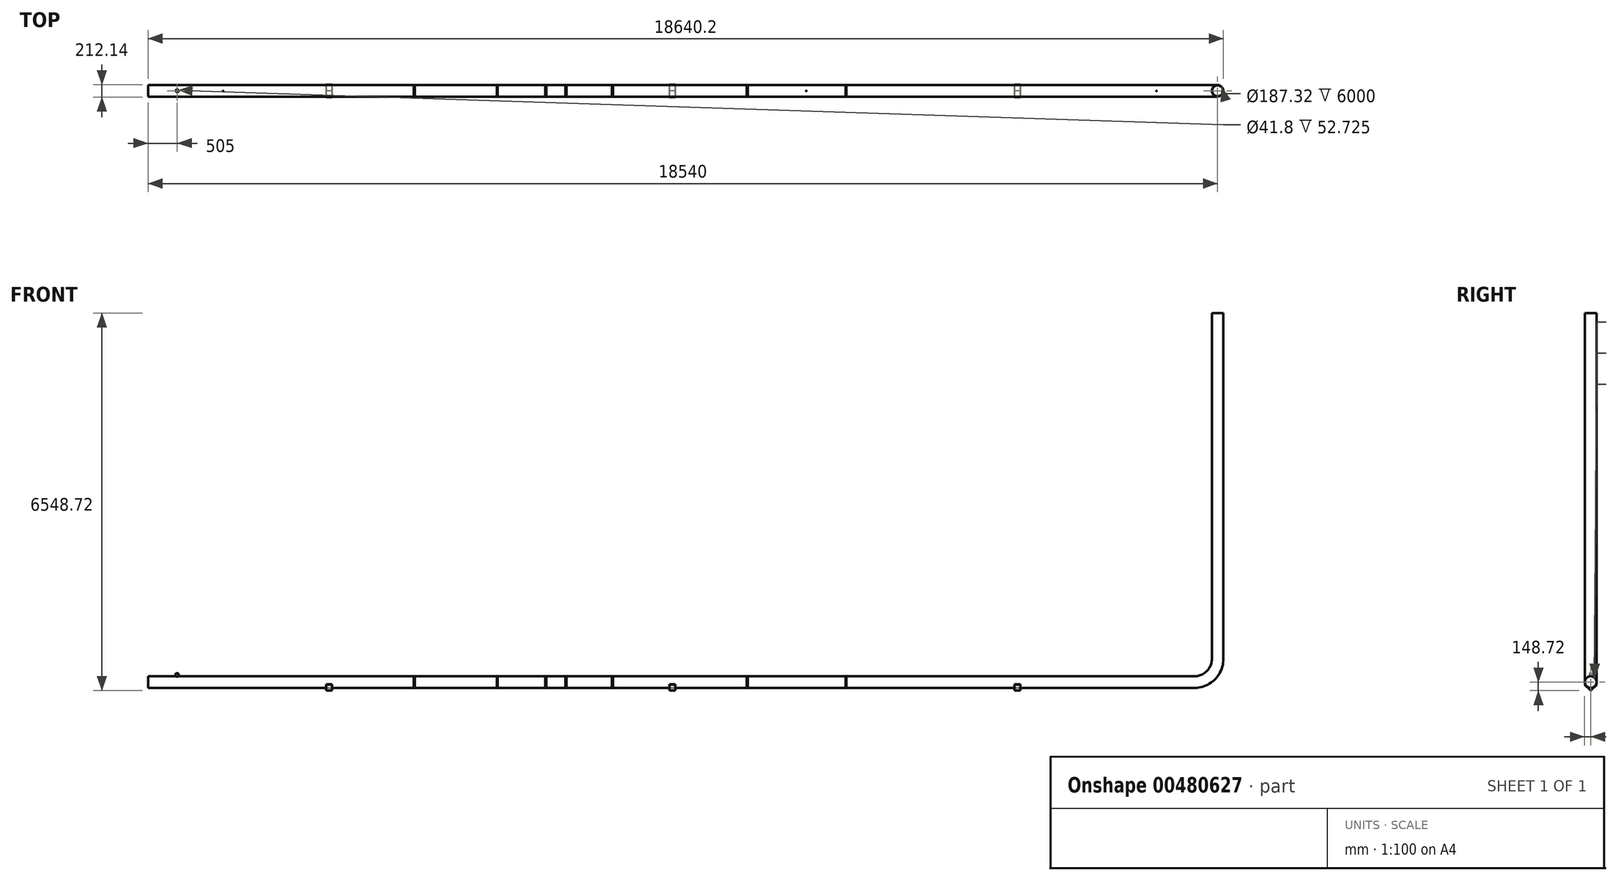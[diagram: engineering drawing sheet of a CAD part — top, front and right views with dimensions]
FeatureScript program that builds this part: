
annotation { "Feature Type Name" : "Feature", "Feature Type Description" : "" }
export const myFeature = defineFeature(function(context is Context, id is Id, definition is map)
    precondition{}
    {
        {
            var Q0;
            Q0=qCreatedBy(makeId("Right.planeOp"),FACE);
            var sketch = newSketch(context, id + "F0", { "sketchPlane" : qUnion([Q0])});
            skCircle(sketch, "E0", {"center": v(0, 0) * mm, "radius": 100.16 * mm});
            skCircle(sketch, "E1", {"center": v(0, 0) * mm, "radius": 93.66 * mm});
            skSolve(sketch);
        }
        {
            var Q0;
            Q0=qCreatedBy(makeId("Front.planeOp"),FACE);
            var sketch = newSketch(context, id + "F1", { "sketchPlane" : qUnion([Q0])});
            skLineSegment(sketch, "E2", {"start": v(0, 0) * mm, "end": v(18140, 0) * mm});
            skArc(sketch, "E3", {"start": v(18140, 0) * mm, "mid": v(18422.84, 117.16) * mm, "end": v(18540, 400) * mm});
            skLineSegment(sketch, "E4", {"start": v(18540, 400) * mm, "end": v(18540, 6400) * mm});
            skSolve(sketch);
        }
        {
            var Q0;
            Q0 = qSketchRegion(id + "F0", true);
            var Q1;
            Q1 = qConstructionFilter(qBodyType(qCreatedBy(id + "F1" ,EDGE), BodyType.WIRE), ConstructionObject.NO);
            sweep(context, id + "F2", {"profiles" : qUnion([Q0]), "path" : qUnion([Q1])});
        }
        {
            var Q0;
            Q0=qCreatedBy(makeId("Top.planeOp"),FACE);
            cPlane(context, id + "F3", {"entities" : qUnion([Q0]), "cplaneType" : CPlaneType.OFFSET, "offset" : 100.18 * mm, "width" : 150 * mm, "height" : 150 * mm});
        }
        {
            var Q0;
            Q0=qCreatedBy(id+"F3.planeOp",FACE);
            var sketch = newSketch(context, id + "F4", { "sketchPlane" : qUnion([Q0])});
            skPoint(sketch, "E5", {"position": v(505, 0) * mm});
            skPoint(sketch, "E6", {"position": v(1300, 0) * mm});
            skPoint(sketch, "E7", {"position": v(3140, 0) * mm});
            skPoint(sketch, "E8", {"position": v(4615, 0) * mm});
            skPoint(sketch, "E9", {"position": v(6055, 0) * mm});
            skPoint(sketch, "E10", {"position": v(6895, 0) * mm});
            skPoint(sketch, "E11", {"position": v(8050, 0) * mm});
            skPoint(sketch, "E12", {"position": v(7245, 0) * mm});
            skPoint(sketch, "E13", {"position": v(9090, 0) * mm});
            skPoint(sketch, "E14", {"position": v(10390, 0) * mm});
            skPoint(sketch, "E15", {"position": v(11410, 0) * mm});
            skPoint(sketch, "E16", {"position": v(12100, 0) * mm});
            skPoint(sketch, "E17", {"position": v(15070, 0) * mm});
            skPoint(sketch, "E18", {"position": v(17480, 0) * mm});
            skSolve(sketch);
        }
        {
            var Q0;
            Q0=qCreatedBy(id+"F3.planeOp",FACE);
            var sketch = newSketch(context, id + "F5", { "sketchPlane" : qUnion([Q0])});
            skCircle(sketch, "E19", {"center": v(505, 0) * mm, "radius": 20.9 * mm});
            skCircle(sketch, "E20", {"center": v(505, 0) * mm, "radius": 24.1 * mm});
            skSolve(sketch);
        }
        {
            var Q0;
            Q0=makeQuery(id+"F5.imprint","IMPRINT",FACE,{"disambiguationData":[TD([[makeQuery(id+"F5.imprint","IMPRINT",EDGE,{"derivedFrom":sQuery(id+"F5.wireOp",EDGE,"E19")}),-1.0]])]});
            extrude(context, id + "F6", {"entities" : qUnion([Q0]), "operationType" : NewBodyOperationType.ADD, "depth" : 50.5 * mm, "offsetDistance" : 25 * mm, "hasSecondDirection" : true, "secondDirectionBound" : SecondDirectionBoundingType.UP_TO_NEXT, "secondDirectionOppositeDirection" : true, "secondDirectionDepth" : 25 * mm});
        }
        {
            var Q0;
            Q0=sQuery(id+"F4.wireOp",VERTEX,"E6");
            var Q1;
            Q1=sQuery(id+"F4.wireOp",VERTEX,"E15");
            var Q2;
            Q2=sQuery(id+"F4.wireOp",VERTEX,"E18");
            var Q3;
            Q3=makeQuery(id+"F2.opSweep","SWEPT_BODY",BODY,{"disambiguationData":[OSD([sQuery(id+"F0.wireOp",EDGE,"E0"),sQuery(id+"F0.wireOp",EDGE,"E1"),sQuery(id+"F1.wireOp",EDGE,"E4")])]});
            hole(context, id + "F7", {"style" : HoleStyle.SIMPLE, "endStyle" : HoleEndStyle.BLIND, "holeDiameter" : 11.3 * mm, "majorDiameter" : 6 * mm, "holeDepth" : 45 * mm, "isTappedThrough" : true, "tappedDepth" : 12 * mm, "tapClearance" : 3, "locations" : qUnion([Q0, Q1, Q2]), "scope" : qUnion([Q3])});
        }
        {
            var Q0;
            Q0=makeQuery(id+"F0.imprint","IMPRINT",FACE,{"disambiguationData":[TD([[makeQuery(id+"F0.imprint","IMPRINT",EDGE,{"derivedFrom":sQuery(id+"F0.wireOp",EDGE,"E1")}),1.0]])]});
            var Q1;
            Q1=sQuery(id+"F4.wireOp",VERTEX,"E7");
            cPlane(context, id + "F8", {"entities" : qUnion([Q0, Q1]), "cplaneType" : CPlaneType.PLANE_POINT, "offset" : 25 * mm, "width" : 150 * mm, "height" : 150 * mm});
        }
        {
            var Q0;
            Q0=qCreatedBy(id+"F8.planeOp",FACE);
            var sketch = newSketch(context, id + "F9", { "sketchPlane" : qUnion([Q0])});
            skLineSegment(sketch, "E21", {"start": v(106.07, -42.65) * mm, "end": v(102.53, -39.12) * mm});
            skLineSegment(sketch, "E22", {"start": v(102.53, -39.12) * mm, "end": v(0, -141.65) * mm});
            skLineSegment(sketch, "E23", {"start": v(0, -141.65) * mm, "end": v(-102.53, -39.12) * mm});
            skLineSegment(sketch, "E24", {"start": v(-102.53, -39.12) * mm, "end": v(-106.07, -42.65) * mm});
            skLineSegment(sketch, "E25", {"start": v(-106.07, -42.65) * mm, "end": v(0, -148.72) * mm});
            skLineSegment(sketch, "E26", {"start": v(0, -148.72) * mm, "end": v(106.07, -42.65) * mm});
            skSolve(sketch);
        }
        {
            var Q0;
            Q0 = qSketchRegion(id + "F9", true);
            extrude(context, id + "F10", {"entities" : qUnion([Q0]), "depth" : 50 * mm, "offsetDistance" : 25 * mm, "hasSecondDirection" : true, "secondDirectionOppositeDirection" : true, "secondDirectionDepth" : 50 * mm});
        }
        {
            var Q0;
            Q0=makeQuery(id+"F0.imprint","IMPRINT",FACE,{"disambiguationData":[TD([[makeQuery(id+"F0.imprint","IMPRINT",EDGE,{"derivedFrom":sQuery(id+"F0.wireOp",EDGE,"E1")}),1.0]])]});
            var Q1;
            Q1=sQuery(id+"F4.wireOp",VERTEX,"E8");
            cPlane(context, id + "F11", {"entities" : qUnion([Q0, Q1]), "cplaneType" : CPlaneType.PLANE_POINT, "offset" : 25 * mm, "width" : 150 * mm, "height" : 150 * mm});
        }
        {
            var Q0;
            Q0=qCreatedBy(id+"F11.planeOp",FACE);
            var sketch = newSketch(context, id + "F12", { "sketchPlane" : qUnion([Q0])});
            skCircle(sketch, "E27", {"center": v(0, 0) * mm, "radius": 100.16 * mm});
            skCircle(sketch, "E28", {"center": v(0, 0) * mm, "radius": 102.16 * mm});
            skSolve(sketch);
        }
        {
            var Q0;
            Q0=makeQuery(id+"F12.imprint","IMPRINT",FACE,{"disambiguationData":[TD([[makeQuery(id+"F12.imprint","IMPRINT",EDGE,{"derivedFrom":sQuery(id+"F12.wireOp",EDGE,"E27")}),-1.0]])]});
            extrude(context, id + "F13", {"entities" : qUnion([Q0]), "depth" : 10 * mm, "offsetDistance" : 25 * mm, "hasSecondDirection" : true, "secondDirectionOppositeDirection" : true, "secondDirectionDepth" : 10 * mm});
        }
        {
            var Q0;
            Q0=makeQuery(id+"F0.imprint","IMPRINT",FACE,{"disambiguationData":[TD([[makeQuery(id+"F0.imprint","IMPRINT",EDGE,{"derivedFrom":sQuery(id+"F0.wireOp",EDGE,"E1")}),1.0]])]});
            var Q1;
            Q1=sQuery(id+"F4.wireOp",VERTEX,"E9");
            cPlane(context, id + "F14", {"entities" : qUnion([Q0, Q1]), "cplaneType" : CPlaneType.PLANE_POINT, "offset" : 25 * mm, "width" : 150 * mm, "height" : 150 * mm});
        }
        {
            var Q0;
            Q0=qCreatedBy(id+"F14.planeOp",FACE);
            var sketch = newSketch(context, id + "F15", { "sketchPlane" : qUnion([Q0])});
            skCircle(sketch, "E29", {"center": v(0, 0) * mm, "radius": 103.16 * mm});
            skCircle(sketch, "E30", {"center": v(0, 0) * mm, "radius": 100.16 * mm});
            skSolve(sketch);
        }
        {
            var Q0;
            Q0 = qSketchRegion(id + "F15", true);
            extrude(context, id + "F16", {"entities" : qUnion([Q0]), "depth" : (14 / 2) * mm, "offsetDistance" : 25 * mm, "hasSecondDirection" : true, "secondDirectionOppositeDirection" : true, "secondDirectionDepth" : (14 / 2) * mm});
        }
        {
            var Q0;
            Q0=makeQuery(id+"F16.opExtrude","SWEPT_FACE",FACE,{"disambiguationData":[OSD([sQuery(id+"F15.wireOp",EDGE,"E29")])]});
            fillet(context, id + "F17", {"entities" : qUnion([Q0]), "radius" : 8 * mm, "tangentPropagation" : true, "allowEdgeOverflow" : false});
        }
        {
            var Q0;
            Q0=makeQuery(id+"F13.opExtrude","SWEPT_BODY",BODY,{"disambiguationData":[OSD([sQuery(id+"F12.wireOp",EDGE,"E27"),sQuery(id+"F12.wireOp",EDGE,"E28")])]});
            var Q1;
            {var subQ0=sQuery(id+"F0.wireOp",EDGE,"E0");Q1=makeQuery(id+"F6.boolean.opBoolean","SPLIT",FACE,{"disambiguationData":[TD([makeQuery(id+"F6.opExtrude","SWEPT_FACE",FACE,{"disambiguationData":[OSD([sQuery(id+"F5.wireOp",EDGE,"E20")])]})])],"derivedFrom":makeQuery(id+"F2.opSweep","SWEPT_FACE",FACE,{"disambiguationData":[OSD([subQ0,sQuery(id+"F1.wireOp",EDGE,"E2")])]})});}
            transform(context, id + "F18", {"entities" : qUnion([Q0]), "transformType" : TransformType.TRANSLATION_DISTANCE, "transformDirection" : qUnion([Q1]), "distance" : 2280 * mm, "makeCopy" : true});
        }
        {
            var Q0;
            Q0=makeQuery(id+"F13.opExtrude","SWEPT_BODY",BODY,{"disambiguationData":[OSD([sQuery(id+"F12.wireOp",EDGE,"E27"),sQuery(id+"F12.wireOp",EDGE,"E28")])]});
            var Q1;
            Q1=sQuery(id+"F1.wireOp",EDGE,"E2");
            transform(context, id + "F19", {"entities" : qUnion([Q0]), "transformType" : TransformType.TRANSLATION_DISTANCE, "transformDirection" : qUnion([Q1]), "distance" : 2630 * mm, "makeCopy" : true});
        }
        {
            var Q0;
            Q0=makeQuery(id+"F13.opExtrude","SWEPT_BODY",BODY,{"disambiguationData":[OSD([sQuery(id+"F12.wireOp",EDGE,"E27"),sQuery(id+"F12.wireOp",EDGE,"E28")])]});
            var Q1;
            Q1=sQuery(id+"F1.wireOp",EDGE,"E2");
            transform(context, id + "F20", {"entities" : qUnion([Q0]), "transformType" : TransformType.TRANSLATION_DISTANCE, "transformDirection" : qUnion([Q1]), "distance" : 3435 * mm, "makeCopy" : true});
        }
        {
            var Q0;
            Q0=makeQuery(id+"F13.opExtrude","SWEPT_BODY",BODY,{"disambiguationData":[OSD([sQuery(id+"F12.wireOp",EDGE,"E27"),sQuery(id+"F12.wireOp",EDGE,"E28")])]});
            var Q1;
            Q1=sQuery(id+"F1.wireOp",EDGE,"E2");
            transform(context, id + "F21", {"entities" : qUnion([Q0]), "transformType" : TransformType.TRANSLATION_DISTANCE, "transformDirection" : qUnion([Q1]), "distance" : 5775 * mm, "makeCopy" : true});
        }
        {
            var Q0;
            Q0=makeQuery(id+"F16.opExtrude","SWEPT_BODY",BODY,{"disambiguationData":[OSD([sQuery(id+"F15.wireOp",EDGE,"E29"),sQuery(id+"F15.wireOp",EDGE,"E30")])]});
            var Q1;
            Q1=sQuery(id+"F1.wireOp",EDGE,"E2");
            transform(context, id + "F22", {"entities" : qUnion([Q0]), "transformType" : TransformType.TRANSLATION_DISTANCE, "transformDirection" : qUnion([Q1]), "distance" : (12100 - 6055) * mm, "makeCopy" : true});
        }
        {
            var Q0;
            Q0=makeQuery(id+"F10.opExtrude","SWEPT_BODY",BODY,{"disambiguationData":[OSD([sQuery(id+"F9.wireOp",EDGE,"E21"),sQuery(id+"F9.wireOp",EDGE,"E22"),sQuery(id+"F9.wireOp",EDGE,"E23"),sQuery(id+"F9.wireOp",EDGE,"E24"),sQuery(id+"F9.wireOp",EDGE,"E25"),sQuery(id+"F9.wireOp",EDGE,"E26")])]});
            var Q1;
            Q1=sQuery(id+"F1.wireOp",EDGE,"E2");
            transform(context, id + "F23", {"entities" : qUnion([Q0]), "transformType" : TransformType.TRANSLATION_DISTANCE, "transformDirection" : qUnion([Q1]), "distance" : (9090 - 3140) * mm, "makeCopy" : true});
        }
        {
            var Q0;
            Q0=makeQuery(id+"F10.opExtrude","SWEPT_BODY",BODY,{"disambiguationData":[OSD([sQuery(id+"F9.wireOp",EDGE,"E21"),sQuery(id+"F9.wireOp",EDGE,"E22"),sQuery(id+"F9.wireOp",EDGE,"E23"),sQuery(id+"F9.wireOp",EDGE,"E24"),sQuery(id+"F9.wireOp",EDGE,"E25"),sQuery(id+"F9.wireOp",EDGE,"E26")])]});
            var Q1;
            Q1=sQuery(id+"F1.wireOp",EDGE,"E2");
            transform(context, id + "F24", {"entities" : qUnion([Q0]), "transformType" : TransformType.TRANSLATION_DISTANCE, "transformDirection" : qUnion([Q1]), "distance" : (15070 - 3140) * mm, "makeCopy" : true});
        }
    });
